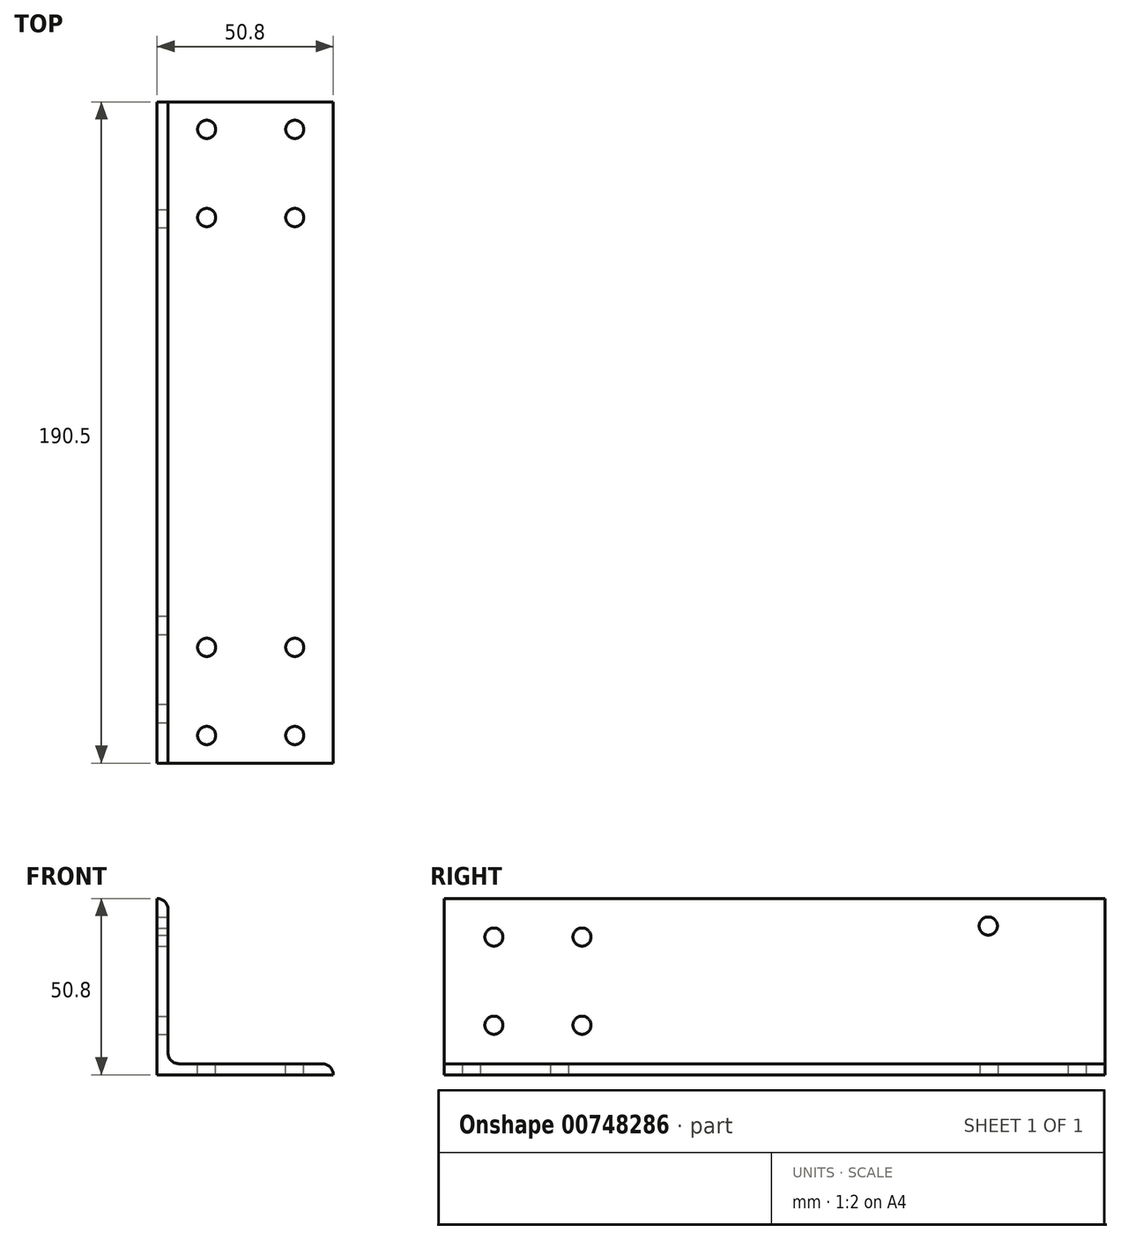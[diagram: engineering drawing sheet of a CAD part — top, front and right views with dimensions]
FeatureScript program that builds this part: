
annotation { "Feature Type Name" : "Feature", "Feature Type Description" : "" }
export const myFeature = defineFeature(function(context is Context, id is Id, definition is map)
    precondition{}
    {
        {
            var Q0;
            Q0=qCreatedBy(makeId("Front.planeOp"),FACE);
            var sketch = newSketch(context, id + "F0", { "sketchPlane" : qUnion([Q0])});
            skLineSegment(sketch, "E0", {"start": v(0, 0) * mm, "end": v(-50.8, 0) * mm});
            skLineSegment(sketch, "E1", {"start": v(-50.8, 0) * mm, "end": v(-50.8, 50.8) * mm});
            skLineSegment(sketch, "E2", {"start": v(-50.8, 50.8) * mm, "end": v(-50.8, 50.8) * mm});
            skLineSegment(sketch, "E3", {"start": v(-47.63, 47.63) * mm, "end": v(-47.63, 6.35) * mm});
            skLineSegment(sketch, "E4", {"start": v(-44.45, 3.18) * mm, "end": v(-3.18, 3.18) * mm});
            skLineSegment(sketch, "E5", {"start": v(0, 0) * mm, "end": v(0, 0) * mm});
            skPoint(sketch, "E6.visualSharp", {"position": v(-47.63, 3.18) * mm});
            skArc(sketch, "E6.filletArc", {"start": v(-47.63, 6.35) * mm, "mid": v(-46.7, 4.1) * mm, "end": v(-44.45, 3.18) * mm});
            skPoint(sketch, "E7.visualSharp", {"position": v(-47.63, 50.8) * mm});
            skArc(sketch, "E7.filletArc", {"start": v(-47.63, 47.63) * mm, "mid": v(-48.55, 49.87) * mm, "end": v(-50.8, 50.8) * mm});
            skPoint(sketch, "E8.visualSharp", {"position": v(0, 3.18) * mm});
            skArc(sketch, "E8.filletArc", {"start": v(0, 0) * mm, "mid": v(-0.93, 2.25) * mm, "end": v(-3.18, 3.18) * mm});
            skSolve(sketch);
        }
        {
            var Q0;
            Q0=qSketchRegion(id+"F0",true);
            extrude(context, id + "F1", {"entities" : qUnion([Q0]), "depth" : 190.5 * mm, "offsetDistance" : 25.4 * mm});
        }
        {
            var Q0;
            Q0=makeQuery(id+"F1.opExtrude","SWEPT_FACE",FACE,{"disambiguationData":[OSD([sQuery(id+"F0.wireOp",EDGE,"E3")])]});
            var sketch = newSketch(context, id + "F2", { "sketchPlane" : qUnion([Q0])});
            skLineSegment(sketch, "E9", {"start": v(-95.25, 6.35) * mm, "end": v(-95.25, 47.63) * mm, "construction": true});
            skLineSegment(sketch, "E10.0", {"start": v(-176.21, -19.05) * mm, "end": v(-176.21, 47.63) * mm, "construction": true});
            skLineSegment(sketch, "E11", {"start": v(-190.5, 26.99) * mm, "end": v(0, 26.99) * mm, "construction": true});
            skCircle(sketch, "E12", {"center": v(-176.21, 14.29) * mm, "radius": 2.62 * mm});
            skLineSegment(sketch, "E13", {"start": v(-190.5, 14.29) * mm, "end": v(0, 14.29) * mm, "construction": true});
            skLineSegment(sketch, "E14", {"start": v(-190.5, 39.69) * mm, "end": v(0, 39.69) * mm, "construction": true});
            skLineSegment(sketch, "E15", {"start": v(-150.81, 47.63) * mm, "end": v(-150.81, 6.35) * mm, "construction": true});
            skCircle(sketch, "E16", {"center": v(-176.21, 39.69) * mm, "radius": 2.62 * mm});
            skCircle(sketch, "E17", {"center": v(-150.81, 39.69) * mm, "radius": 2.62 * mm});
            skCircle(sketch, "E18", {"center": v(-150.81, 14.29) * mm, "radius": 2.62 * mm});
            skLineSegment(sketch, "E19", {"start": v(-190.5, 42.86) * mm, "end": v(0, 42.86) * mm, "construction": true});
            skCircle(sketch, "E20", {"center": v(-33.68, 42.86) * mm, "radius": 2.62 * mm});
            skSolve(sketch);
        }
        {
            var Q0;
            Q0=qSketchRegion(id+"F2",true);
            extrude(context, id + "F3", {"entities" : qUnion([Q0]), "operationType" : NewBodyOperationType.REMOVE, "endBound" : BoundingType.THROUGH_ALL, "oppositeDirection" : true, "depth" : 25.4 * mm, "offsetDistance" : 25.4 * mm});
        }
        {
            var Q0;
            Q0=makeQuery(id+"F1.opExtrude","SWEPT_FACE",FACE,{"disambiguationData":[OSD([sQuery(id+"F0.wireOp",EDGE,"E4")])]});
            var sketch = newSketch(context, id + "F4", { "sketchPlane" : qUnion([Q0])});
            skLineSegment(sketch, "E21", {"start": v(-23.81, -190.5) * mm, "end": v(-23.81, 0) * mm, "construction": true});
            skLineSegment(sketch, "E22", {"start": v(-3.17, -182.56) * mm, "end": v(-44.45, -182.56) * mm, "construction": true});
            skCircle(sketch, "E23", {"center": v(-36.51, -182.56) * mm, "radius": 2.62 * mm});
            skLineSegment(sketch, "E24", {"start": v(-44.45, -7.94) * mm, "end": v(-3.18, -7.94) * mm, "construction": true});
            skCircle(sketch, "E25", {"center": v(-36.51, -7.94) * mm, "radius": 2.62 * mm});
            skLineSegment(sketch, "E26", {"start": v(-36.51, -190.5) * mm, "end": v(-36.51, 0) * mm, "construction": true});
            skLineSegment(sketch, "E27", {"start": v(-44.45, -157.16) * mm, "end": v(-3.17, -157.16) * mm, "construction": true});
            skLineSegment(sketch, "E28", {"start": v(-11.11, -190.5) * mm, "end": v(-11.11, 0) * mm, "construction": true});
            skLineSegment(sketch, "E29", {"start": v(-44.45, -33.34) * mm, "end": v(-3.17, -33.34) * mm, "construction": true});
            skCircle(sketch, "E30", {"center": v(-11.11, -7.94) * mm, "radius": 2.62 * mm});
            skCircle(sketch, "E31", {"center": v(-36.51, -33.34) * mm, "radius": 2.62 * mm});
            skCircle(sketch, "E32", {"center": v(-11.11, -33.34) * mm, "radius": 2.62 * mm});
            skCircle(sketch, "E33", {"center": v(-36.51, -157.16) * mm, "radius": 2.62 * mm});
            skCircle(sketch, "E34", {"center": v(-11.11, -182.56) * mm, "radius": 2.62 * mm});
            skCircle(sketch, "E35", {"center": v(-11.11, -157.16) * mm, "radius": 2.62 * mm});
            skSolve(sketch);
        }
        {
            var Q0;
            Q0=qSketchRegion(id+"F4",true);
            extrude(context, id + "F5", {"entities" : qUnion([Q0]), "operationType" : NewBodyOperationType.REMOVE, "endBound" : BoundingType.THROUGH_ALL, "oppositeDirection" : true, "depth" : 25.4 * mm, "offsetDistance" : 25.4 * mm});
        }
    });
